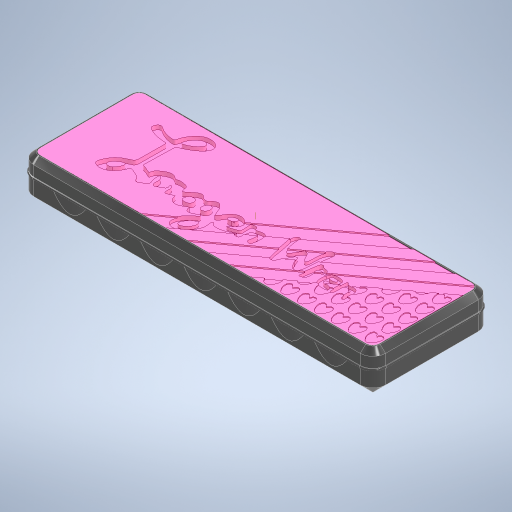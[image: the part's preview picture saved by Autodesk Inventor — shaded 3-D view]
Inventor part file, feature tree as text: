
AUTODESK INVENTOR PART (.ipt)
format: ipt  version: 2024.1 (Build 281209000, 209)  size: 2,139,648 bytes
history: native  units: mm
features: projected_geometry x29, extrude x20, fillet x11, chamfer x5, other x4, pattern_circular x2, sketch x2, plane x1, pattern_linear x1, mirror x1
ambient origin geometry x8: Origin, YZ Plane, XZ Plane, XY Plane, X Axis, Y Axis, Z Axis, Center Point
bodies: Body1 (feature_tree), Body2 (feature_tree), Body3 (feature_tree)
feature tree (76):
  other  "case"
  extrude  "Extrusion1"  Depth=56.0mm
  extrude  "Extrusion2"  Depth=28.0mm
  extrude  "Extrusion3"  Depth=18.0mm TaperAngle=0.0deg
  fillet  "Fillet1"  Radius=2.0mm
  fillet  "Fillet2"  Radius=4.0mm
  fillet  "Fillet3"  Radius=20.0mm
  pattern_circular  "Circular Pattern1"  [2 undecoded]
  fillet  "Fillet4"  Radius=20.0mm
  chamfer  "Chamfer1"  Distance=96.0mm
  extrude  "Extrusion4"  Depth=65.0mm
  chamfer  "Chamfer2"  Distance=74.2mm
  extrude  "Extrusion5"  Depth=12.0mm
  pattern_circular  "Circular Pattern2"  [2 undecoded]
  fillet  "Fillet5"  Radius=12.4mm
  fillet  "Fillet6"  Radius=0.95mm
  fillet  "Fillet10"  Radius=0.95mm
  fillet  "Fillet11"  Radius=2.0mm
  fillet  "Fillet12"  Radius=3.7mm
  extrude  "Extrusion6"  Depth=17.6mm TaperAngle=0.0deg
  plane  "Work Plane1"
  extrude  "Extrusion7"  Depth=25.0mm
  extrude  "Extrusion8"  Depth=16.6mm
  extrude  "Extrusion9"  Depth=4.0mm
  fillet  "Fillet8"  Radius=3.0mm
  extrude  "Extrusion10"  Depth=4.0mm
  pattern_linear  "Rectangular Pattern1"  Count1=2 Spacing1=180.0deg
  mirror  "Mirror1"
  extrude  "Extrusion11"  Depth=6.0mm
  extrude  "Extrusion15"  Depth=6.0mm TaperAngle=45.0deg
  extrude  "Extrusion16"  Depth=1.3mm
  chamfer  "Chamfer4"  Distance=5.0mm
  extrude  "Extrusion18"  Depth=3.0mm TaperAngle=45.0deg
  extrude  "Extrusion19"  Depth=6.0mm
  extrude  "Extrusion12"  Depth=6.5mm
  extrude  "Extrusion13"  Depth=6.5mm
  extrude  "Extrusion14"  Depth=22.0mm
  extrude  "Extrusion17"  Depth=2.0mm TaperAngle=0.0deg
  chamfer  "Chamfer5"  Distance=20.0mm Angle=360.0deg
  chamfer  "Chamfer6"  Distance=6.5mm
  extrude  "Extrusion20"  Depth=6.5mm
  fillet  "Fillet13"  Radius=2.0mm
  projected_geometry  "Projected Loop1"
  projected_geometry  "Projected Loop5"
  other  "Work Axis1"
  projected_geometry  "Projected Loop7"
  other  "lid"
  projected_geometry  "Projected Loop8"
  projected_geometry  "Projected Loop9"
  projected_geometry  "Projected Loop10"
  projected_geometry  "Projected Loop11"
  sketch  "Sketch15"  dims[d0=167.0mm d1=56.0mm]
  sketch  "Sketch16"  dims[d2=83.5mm d3=28.0mm d4=18.0mm d5=0.0mm d6=2.0mm d8=4.0mm d9=20.0mm d10=4.0mm d11=20.0mm d12=96.0mm d13=65.0mm d14=74.2mm d15=12.0mm d16=14.3mm d17=12.4mm d18=0.95mm d19=0.95mm d20=2.0mm d21=3.7mm d22=17.6mm d23=0.0mm d24=25.0mm d27=16.6mm d28=-1.745329mm d29=4.0mm d30=3.0mm d31=4.0mm d32=20.0mm d33=180.0deg d35=6.0mm d36=6.0mm d37=2.0mm d38=45.0deg d39=1.3mm d40=5.0mm d41=0.0mm d42=3.0mm d43=2.0mm d44=45.0deg d45=6.0mm d46=6.5mm d47=6.5mm d48=22.0mm d49=2.0mm d50=0.0mm d51=20.0mm d52=360.0deg d54=6.5mm d55=6.5mm d56=2.0mm d57=3.0mm d59=6.5mm d60=6.45mm d61=1.0mm d62=3.0mm d63=0.0mm d64=3.1mm d65=0.0mm d69=1.8mm d70=0.0mm d71=0.5mm d72=1.0mm d73=0.0mm d74=0.5mm d75=60.0mm d76=20.0mm d77=29.0mm d79=8.5mm d80=-1.745329mm d82=70.0mm d84=124.0mm d85=55.0mm d86=1.0mm d89=2.0mm d90=0.0mm d91=0.6mm d92=0.0mm d93=30.0deg d94=1.0mm d95=6.0mm d96=6.0mm d97=7.0mm d98=6.0mm d99=6.0mm d101=1.0mm d108=3.0mm d109=3.0mm d110=0.4mm d111=0.0mm d112=1.6mm d113=1.6mm d114=1.1mm d115=1.1mm d116=7.0mm d117=3.0mm d119=2.0mm d120=1.1mm d121=1.1mm d122=1.5mm d123=1.5mm d124=1.5mm d125=1.0mm d126=1.1mm d127=1.1mm d128=1.8mm d131=2.0mm d132=1.5mm d133=1.5mm d140=50.0mm d142=8.0mm d143=60.0mm d145=8.0mm d148=0.0mm d149=0.0mm d150=0.0mm d151=0.0mm d152=3.5mm d153=0.0mm d154=2.5mm d155=2.0mm d156=45.0deg d158=0.4mm d159=0.4mm d160=0.0mm d163=3.0mm d164=1.5mm d165=0.4mm d166=0.0mm d167=3.1mm d168=0.0mm d169=1.5mm d170=2.0mm d171=45.0deg d172=1.5mm d173=2.0mm d174=45.0deg d175=8.0mm d176=8.0mm d177=45.0mm d178=16.0mm d179=3.0mm d180=3.0mm d181=3.0mm d182=0.0mm d183=0.0mm d184=1.0mm]
  other  "lid-part2"
  projected_geometry  "Projected Loop12"
  projected_geometry  "Projected Loop13"
  projected_geometry  "Projected Loop14"
  projected_geometry  "Projected Loop15"
  projected_geometry  "Projected Loop16"
  projected_geometry  "Projected Loop17"
  projected_geometry  "Projected Loop18"
  projected_geometry  "Projected Loop19"
  projected_geometry  "Projected Loop20"
  projected_geometry  "Projected Loop21"
  projected_geometry  "Projected Loop22"
  projected_geometry  "Projected Loop23"
  projected_geometry  "Projected Loop24"
  projected_geometry  "Projected Loop25"
  projected_geometry  "Projected Loop26"
  projected_geometry  "Projected Loop27"
  projected_geometry  "Projected Loop28"
  projected_geometry  "Projected Loop29"
  projected_geometry  "Projected Loop30"
  projected_geometry  "Projected Loop31"
  projected_geometry  "Projected Loop32"
  projected_geometry  "Projected Loop33"
note: 4 required parameter values undecoded (feature->parameter linkage not recoverable at this tier; creation-order binding heuristic only, values carry confidence <= 0.55)
